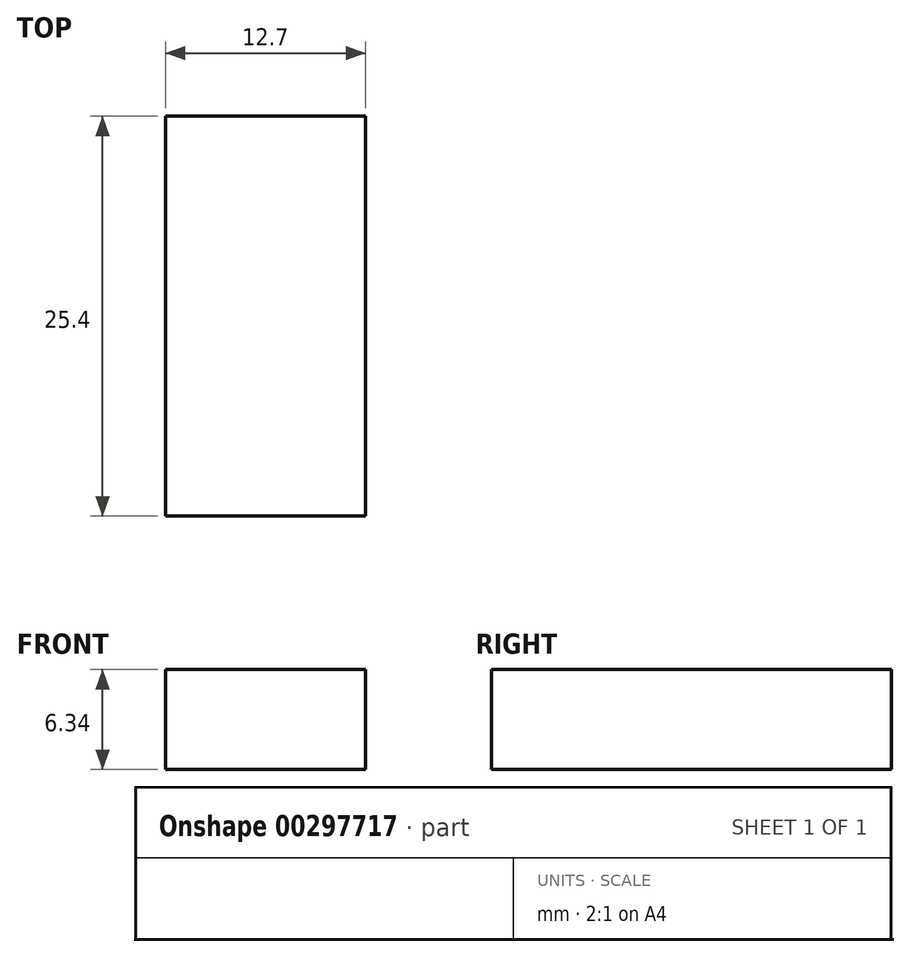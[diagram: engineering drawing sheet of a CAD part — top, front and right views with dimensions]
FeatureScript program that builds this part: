
annotation { "Feature Type Name" : "Feature", "Feature Type Description" : "" }
export const myFeature = defineFeature(function(context is Context, id is Id, definition is map)
    precondition{}
    {
        {
            var Q0;
            Q0=qCreatedBy(makeId("Front.planeOp"),FACE);
            var sketch = newSketch(context, id + "F0", { "sketchPlane" : qUnion([Q0])});
            skLineSegment(sketch, "E0.bottom", {"start": v(6.35, 3.18) * mm, "end": v(-6.35, 3.18) * mm});
            skLineSegment(sketch, "E0.top", {"start": v(6.35, -3.17) * mm, "end": v(-6.35, -3.17) * mm});
            skLineSegment(sketch, "E0.left", {"start": v(6.35, 3.18) * mm, "end": v(6.35, -3.17) * mm});
            skLineSegment(sketch, "E0.right", {"start": v(-6.35, 3.18) * mm, "end": v(-6.35, -3.18) * mm});
            skPoint(sketch, "E0.middle", {"position": v(0, 0) * mm});
            skSolve(sketch);
        }
        {
            var Q0;
            Q0 = qSketchRegion(id + "F0", true);
            extrude(context, id + "F1", {"entities" : qUnion([Q0]), "depth" : 25.4 * mm});
        }
    });
